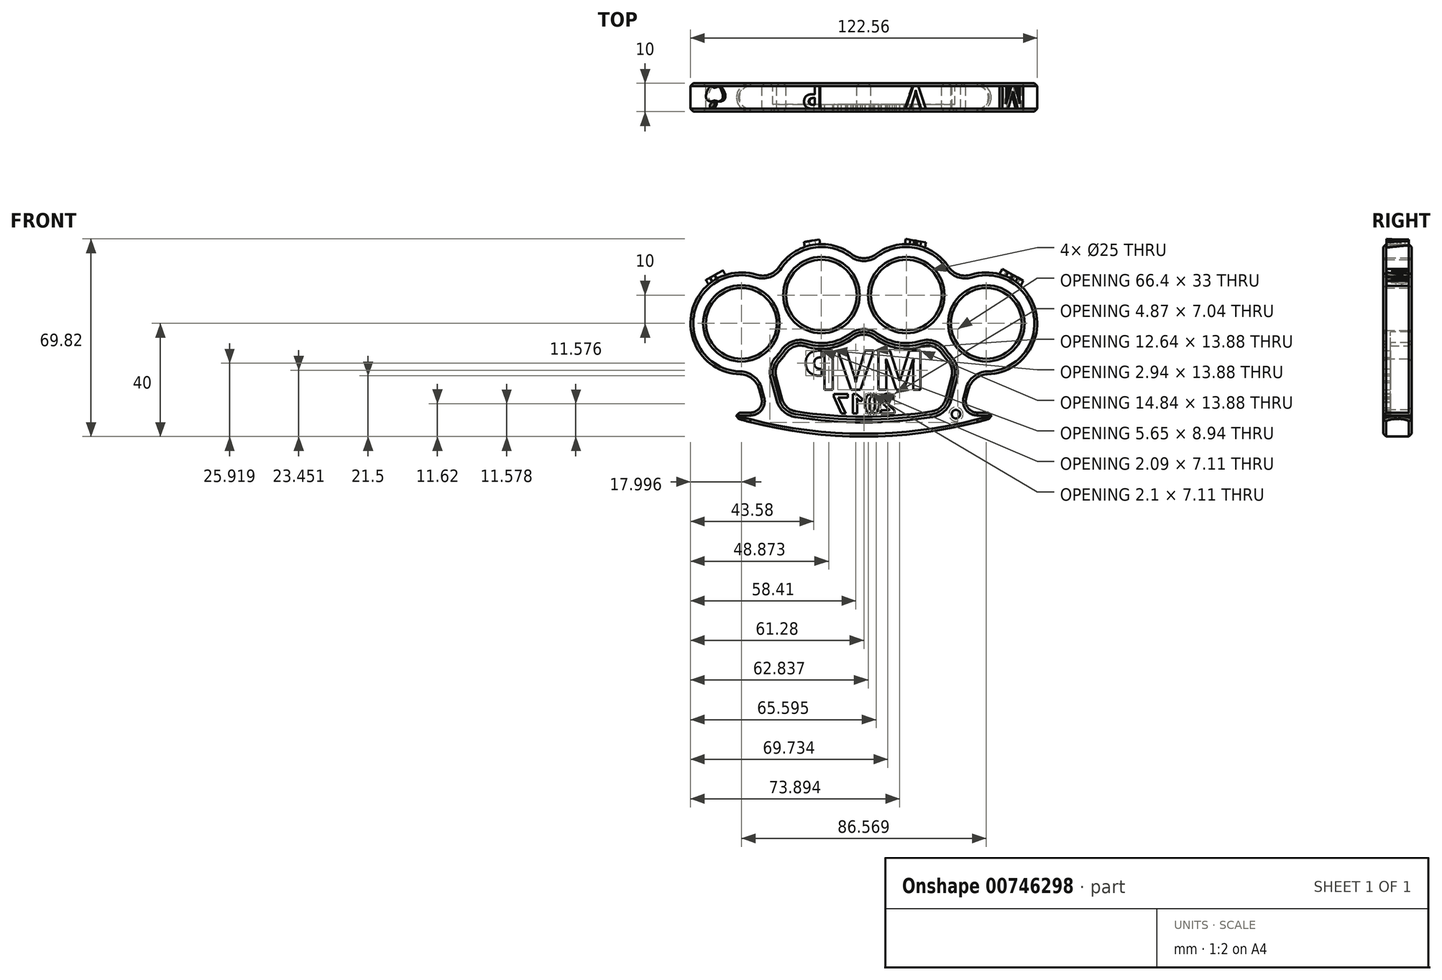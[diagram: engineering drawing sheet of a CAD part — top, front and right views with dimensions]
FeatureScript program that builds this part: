
annotation { "Feature Type Name" : "Feature", "Feature Type Description" : "" }
export const myFeature = defineFeature(function(context is Context, id is Id, definition is map)
    precondition{}
    {
        {
            var Q0;
            Q0=qCreatedBy(makeId("Front.planeOp"),FACE);
            var sketch = newSketch(context, id + "F0", { "sketchPlane" : qUnion([Q0])});
            skCircle(sketch, "E0", {"center": v(-43.28, 0) * mm, "radius": 12.5 * mm});
            skCircle(sketch, "E1", {"center": v(-15, 10) * mm, "radius": 12.5 * mm});
            skCircle(sketch, "E2", {"center": v(15, 10) * mm, "radius": 12.5 * mm});
            skCircle(sketch, "E3", {"center": v(43.28, 0) * mm, "radius": 12.5 * mm});
            skLineSegment(sketch, "E4", {"start": v(0, 38.87) * mm, "end": v(0, -56.1) * mm, "construction": true});
            skArc(sketch, "E5", {"start": v(-32.46, 14.38) * mm, "mid": v(-60.95, 3.43) * mm, "end": v(-38.63, -17.39) * mm});
            skArc(sketch, "E6", {"start": v(25.83, -4.38) * mm, "mid": v(28.5, -10.27) * mm, "end": v(33.1, -14.84) * mm});
            skArc(sketch, "E7.trimOffspring", {"start": v(-25.83, -4.38) * mm, "mid": v(-11.96, -7.74) * mm, "end": v(0, 0.05) * mm});
            skArc(sketch, "E8.trimOffspring", {"start": v(32.46, 14.38) * mm, "mid": v(18.04, 27.74) * mm, "end": v(0, 19.95) * mm});
            skArc(sketch, "E9.trimOffspring", {"start": v(0, 19.95) * mm, "mid": v(-18.04, 27.74) * mm, "end": v(-32.46, 14.38) * mm});
            skArc(sketch, "E10.trimOffspring", {"start": v(0, 0.05) * mm, "mid": v(11.96, -7.74) * mm, "end": v(25.83, -4.38) * mm});
            skArc(sketch, "E11", {"start": v(-45, -33.54) * mm, "mid": v(0, -40) * mm, "end": v(45, -33.54) * mm});
            skLineSegment(sketch, "E12", {"start": v(-45, -33.54) * mm, "end": v(-45, -31.54) * mm});
            skLineSegment(sketch, "E13", {"start": v(-36.18, -26.5) * mm, "end": v(-38.63, -17.39) * mm});
            skLineSegment(sketch, "E14", {"start": v(-45, -31.54) * mm, "end": v(-40.05, -31.54) * mm});
            skLineSegment(sketch, "E15.MirrorCS", {"start": v(45, -33.54) * mm, "end": v(45, -31.54) * mm});
            skPoint(sketch, "E16.visualSharp", {"position": v(-34.83, -31.54) * mm});
            skArc(sketch, "E16.filletArc", {"start": v(-40.05, -31.54) * mm, "mid": v(-36.87, -29.98) * mm, "end": v(-36.18, -26.5) * mm});
            skLineSegment(sketch, "E17.MirrorCS", {"start": v(36.18, -26.5) * mm, "end": v(38.63, -17.39) * mm});
            skLineSegment(sketch, "E18.MirrorCS", {"start": v(45, -31.54) * mm, "end": v(40.05, -31.54) * mm});
            skArc(sketch, "E19.MirrorCS", {"start": v(40.05, -31.54) * mm, "mid": v(36.87, -29.98) * mm, "end": v(36.18, -26.5) * mm});
            skArc(sketch, "E20", {"start": v(-28.68, -31.3) * mm, "mid": v(0, -34) * mm, "end": v(28.68, -31.3) * mm});
            skLineSegment(sketch, "E21", {"start": v(-28.68, -31.3) * mm, "end": v(-33.1, -14.84) * mm});
            skLineSegment(sketch, "E22", {"start": v(28.68, -31.3) * mm, "end": v(33.1, -14.84) * mm});
            skArc(sketch, "E23.trimOffspring", {"start": v(-33.1, -14.84) * mm, "mid": v(-28.5, -10.27) * mm, "end": v(-25.83, -4.38) * mm});
            skArc(sketch, "E24.trimOffspring", {"start": v(38.63, -17.39) * mm, "mid": v(60.95, 3.43) * mm, "end": v(32.46, 14.38) * mm});
            skSolve(sketch);
        }
        {
            var Q0;
            Q0=makeQuery(id+"F0.imprint","IMPRINT",FACE,{"disambiguationData":[TD([[makeQuery(id+"F0.imprint","IMPRINT",EDGE,{"derivedFrom":sQuery(id+"F0.wireOp",EDGE,"E0")}),-1.0]])]});
            extrude(context, id + "F1", {"entities" : qUnion([Q0]), "depth" : 10 * mm, "offsetDistance" : 25 * mm});
        }
        {
            var Q0;
            Q0=makeQuery(id+"F1.opExtrude","CAP_EDGE",EDGE,{"disambiguationData":[OSD([sQuery(id+"F0.wireOp",EDGE,"E12")])],"isStart":false});
            var Q1;
            Q1=makeQuery(id+"F1.opExtrude","CAP_EDGE",EDGE,{"disambiguationData":[OSD([sQuery(id+"F0.wireOp",EDGE,"E12")])],"isStart":true});
            var Q2;
            Q2=makeQuery(id+"F1.opExtrude","CAP_EDGE",EDGE,{"disambiguationData":[OSD([sQuery(id+"F0.wireOp",EDGE,"E15.MirrorCS")])],"isStart":false});
            var Q3;
            Q3=makeQuery(id+"F1.opExtrude","CAP_EDGE",EDGE,{"disambiguationData":[OSD([sQuery(id+"F0.wireOp",EDGE,"E15.MirrorCS")])],"isStart":true});
            fillet(context, id + "F2", {"entities" : qUnion([Q0, Q1, Q2, Q3]), "radius" : 5 * mm, "tangentPropagation" : true, "allowEdgeOverflow" : false});
        }
        {
            var Q0;
            Q0=makeQuery(id+"F1.opExtrude","SWEPT_EDGE",EDGE,{"disambiguationData":[OSD([sQuery(id+"F0.wireOp",EDGE,"E7.trimOffspring"),sQuery(id+"F0.wireOp",EDGE,"E23.trimOffspring")])]});
            var Q1;
            Q1=makeQuery(id+"F1.opExtrude","SWEPT_EDGE",EDGE,{"disambiguationData":[OSD([sQuery(id+"F0.wireOp",EDGE,"E7.trimOffspring"),sQuery(id+"F0.wireOp",EDGE,"E10.trimOffspring")])]});
            var Q2;
            Q2=makeQuery(id+"F1.opExtrude","SWEPT_EDGE",EDGE,{"disambiguationData":[OSD([sQuery(id+"F0.wireOp",EDGE,"E6"),sQuery(id+"F0.wireOp",EDGE,"E10.trimOffspring")])]});
            var Q3;
            Q3=makeQuery(id+"F1.opExtrude","SWEPT_EDGE",EDGE,{"disambiguationData":[OSD([sQuery(id+"F0.wireOp",EDGE,"E6"),sQuery(id+"F0.wireOp",EDGE,"E22")])]});
            var Q4;
            Q4=makeQuery(id+"F1.opExtrude","SWEPT_EDGE",EDGE,{"disambiguationData":[OSD([sQuery(id+"F0.wireOp",EDGE,"E21"),sQuery(id+"F0.wireOp",EDGE,"E23.trimOffspring")])]});
            var Q5;
            Q5=makeQuery(id+"F1.opExtrude","SWEPT_EDGE",EDGE,{"disambiguationData":[OSD([sQuery(id+"F0.wireOp",EDGE,"E8.trimOffspring"),sQuery(id+"F0.wireOp",EDGE,"E24.trimOffspring")])]});
            var Q6;
            Q6=makeQuery(id+"F1.opExtrude","SWEPT_EDGE",EDGE,{"disambiguationData":[OSD([sQuery(id+"F0.wireOp",EDGE,"E8.trimOffspring"),sQuery(id+"F0.wireOp",EDGE,"E9.trimOffspring")])]});
            var Q7;
            Q7=makeQuery(id+"F1.opExtrude","SWEPT_EDGE",EDGE,{"disambiguationData":[OSD([sQuery(id+"F0.wireOp",EDGE,"E5"),sQuery(id+"F0.wireOp",EDGE,"E9.trimOffspring")])]});
            var Q8;
            Q8=makeQuery(id+"F1.opExtrude","SWEPT_EDGE",EDGE,{"disambiguationData":[OSD([sQuery(id+"F0.wireOp",EDGE,"E20"),sQuery(id+"F0.wireOp",EDGE,"E21")])]});
            var Q9;
            Q9=makeQuery(id+"F1.opExtrude","SWEPT_EDGE",EDGE,{"disambiguationData":[OSD([sQuery(id+"F0.wireOp",EDGE,"E20"),sQuery(id+"F0.wireOp",EDGE,"E22")])]});
            var Q10;
            Q10=makeQuery(id+"F1.opExtrude","SWEPT_EDGE",EDGE,{"disambiguationData":[OSD([sQuery(id+"F0.wireOp",EDGE,"E5"),sQuery(id+"F0.wireOp",EDGE,"E13")])]});
            var Q11;
            Q11=makeQuery(id+"F1.opExtrude","SWEPT_EDGE",EDGE,{"disambiguationData":[OSD([sQuery(id+"F0.wireOp",EDGE,"E17.MirrorCS"),sQuery(id+"F0.wireOp",EDGE,"E24.trimOffspring")])]});
            fillet(context, id + "F3", {"entities" : qUnion([Q0, Q1, Q2, Q3, Q4, Q5, Q6, Q7, Q8, Q9, Q10, Q11]), "radius" : 7 * mm, "tangentPropagation" : true, "allowEdgeOverflow" : false});
        }
        {
            var Q0;
            Q0=qCreatedBy(makeId("Front.planeOp"),FACE);
            cPlane(context, id + "F4", {"entities" : qUnion([Q0]), "cplaneType" : CPlaneType.OFFSET, "offset" : 5 * mm, "width" : 150 * mm, "height" : 150 * mm});
        }
        {
            var Q0;
            Q0=makeQuery(id+"F1.opExtrude","CAP_FACE",FACE,{"disambiguationData":[OSD([sQuery(id+"F0.wireOp",EDGE,"E0"),sQuery(id+"F0.wireOp",EDGE,"E1"),sQuery(id+"F0.wireOp",EDGE,"E2"),sQuery(id+"F0.wireOp",EDGE,"E3"),sQuery(id+"F0.wireOp",EDGE,"E5"),sQuery(id+"F0.wireOp",EDGE,"E6"),sQuery(id+"F0.wireOp",EDGE,"E7.trimOffspring"),sQuery(id+"F0.wireOp",EDGE,"E8.trimOffspring"),sQuery(id+"F0.wireOp",EDGE,"E9.trimOffspring"),sQuery(id+"F0.wireOp",EDGE,"E10.trimOffspring"),sQuery(id+"F0.wireOp",EDGE,"E11"),sQuery(id+"F0.wireOp",EDGE,"E12"),sQuery(id+"F0.wireOp",EDGE,"E13"),sQuery(id+"F0.wireOp",EDGE,"E14"),sQuery(id+"F0.wireOp",EDGE,"E15.MirrorCS"),sQuery(id+"F0.wireOp",EDGE,"E16.filletArc"),sQuery(id+"F0.wireOp",EDGE,"E17.MirrorCS"),sQuery(id+"F0.wireOp",EDGE,"E18.MirrorCS"),sQuery(id+"F0.wireOp",EDGE,"E19.MirrorCS"),sQuery(id+"F0.wireOp",EDGE,"E20"),sQuery(id+"F0.wireOp",EDGE,"E21"),sQuery(id+"F0.wireOp",EDGE,"E22"),sQuery(id+"F0.wireOp",EDGE,"E23.trimOffspring"),sQuery(id+"F0.wireOp",EDGE,"E24.trimOffspring")])],"isStart":false});
            var sketch = newSketch(context, id + "F5", { "sketchPlane" : qUnion([Q0])});
            skLineSegment(sketch, "E25.0", {"start": v(-29.84, -26.99) * mm, "end": v(-31.96, -19.07) * mm});
            skArc(sketch, "E25.1", {"start": v(-24.18, -32.1) * mm, "mid": v(-27.76, -30.38) * mm, "end": v(-29.84, -26.99) * mm});
            skArc(sketch, "E25.2", {"start": v(-24.18, -32.1) * mm, "mid": v(0, -34) * mm, "end": v(24.18, -32.1) * mm});
            skArc(sketch, "E25.3", {"start": v(29.84, -26.99) * mm, "mid": v(27.76, -30.38) * mm, "end": v(24.18, -32.1) * mm});
            skLineSegment(sketch, "E25.4", {"start": v(29.84, -26.99) * mm, "end": v(31.96, -19.07) * mm});
            skArc(sketch, "E25.5", {"start": v(30.26, -12.43) * mm, "mid": v(31.98, -15.53) * mm, "end": v(31.96, -19.07) * mm});
            skArc(sketch, "E25.6", {"start": v(20.38, -7.18) * mm, "mid": v(24.8, -7.26) * mm, "end": v(28.3, -9.98) * mm});
            skArc(sketch, "E25.7", {"start": v(4.2, -4.4) * mm, "mid": v(11.96, -7.74) * mm, "end": v(20.38, -7.18) * mm});
            skArc(sketch, "E25.8", {"start": v(-4.2, -4.4) * mm, "mid": v(0, -3) * mm, "end": v(4.2, -4.4) * mm});
            skArc(sketch, "E25.9", {"start": v(-20.38, -7.18) * mm, "mid": v(-11.96, -7.74) * mm, "end": v(-4.2, -4.4) * mm});
            skArc(sketch, "E25.10", {"start": v(-28.3, -9.98) * mm, "mid": v(-24.8, -7.26) * mm, "end": v(-20.38, -7.18) * mm});
            skArc(sketch, "E25.11", {"start": v(-31.96, -19.07) * mm, "mid": v(-31.98, -15.53) * mm, "end": v(-30.26, -12.43) * mm});
            skArc(sketch, "E25.12", {"start": v(-30.26, -12.43) * mm, "mid": v(-29.23, -11.25) * mm, "end": v(-28.3, -9.98) * mm});
            skArc(sketch, "E25.13", {"start": v(28.3, -9.98) * mm, "mid": v(29.23, -11.25) * mm, "end": v(30.26, -12.43) * mm});
            skSolve(sketch);
        }
        {
            var Q0;
            Q0=qSketchRegion(id+"F5",true);
            extrude(context, id + "F6", {"entities" : qUnion([Q0]), "operationType" : NewBodyOperationType.ADD, "oppositeDirection" : true, "depth" : 2.5 * mm, "offsetDistance" : 25 * mm});
        }
        {
            var Q0;
            Q0=makeQuery(id+"F6.opExtrude","CAP_FACE",FACE,{"disambiguationData":[OSD([sQuery(id+"F5.wireOp",EDGE,"E25.0"),sQuery(id+"F5.wireOp",EDGE,"E25.1"),sQuery(id+"F5.wireOp",EDGE,"E25.2"),sQuery(id+"F5.wireOp",EDGE,"E25.3"),sQuery(id+"F5.wireOp",EDGE,"E25.4"),sQuery(id+"F5.wireOp",EDGE,"E25.5"),sQuery(id+"F5.wireOp",EDGE,"E25.6"),sQuery(id+"F5.wireOp",EDGE,"E25.7"),sQuery(id+"F5.wireOp",EDGE,"E25.8"),sQuery(id+"F5.wireOp",EDGE,"E25.9"),sQuery(id+"F5.wireOp",EDGE,"E25.10"),sQuery(id+"F5.wireOp",EDGE,"E25.11"),sQuery(id+"F5.wireOp",EDGE,"E25.12"),sQuery(id+"F5.wireOp",EDGE,"E25.13")])],"isStart":false});
            var sketch = newSketch(context, id + "F7", { "sketchPlane" : qUnion([Q0])});
            skText(sketch, "E26", { "text": "MVP", "fontName": "OpenSans-Bold.ttf"});
            skText(sketch, "E27", { "text": "2017", "fontName": "OpenSans-Bold.ttf"});
            const initialGuessF7  = {"E26": [-0.02178, -0.02349, 1, 0, 0.014], "E27": [-0.01126, -0.0319, 1, 0, 0.007]};
            skSetInitialGuess(sketch, initialGuessF7);
            skSolve(sketch);
        }
        {
            var Q0;
            Q0=qSketchRegion(id+"F7",true);
            extrude(context, id + "F8", {"entities" : qUnion([Q0]), "operationType" : NewBodyOperationType.REMOVE, "oppositeDirection" : true, "depth" : 25 * mm, "offsetDistance" : 25 * mm});
        }
        {
            var Q0;
            Q0=makeQuery(id+"F1.opExtrude","CAP_EDGE",EDGE,{"disambiguationData":[OSD([sQuery(id+"F0.wireOp",EDGE,"E5")])],"isStart":false});
            var Q1;
            Q1=makeQuery(id+"F1.opExtrude","CAP_EDGE",EDGE,{"disambiguationData":[OSD([sQuery(id+"F0.wireOp",EDGE,"E11")])],"isStart":false});
            var Q2;
            Q2=makeQuery(id+"F1.opExtrude","CAP_EDGE",EDGE,{"disambiguationData":[OSD([sQuery(id+"F0.wireOp",EDGE,"E21")])],"isStart":false});
            var Q3;
            Q3=makeQuery(id+"F1.opExtrude","CAP_EDGE",EDGE,{"disambiguationData":[OSD([sQuery(id+"F0.wireOp",EDGE,"E0")])],"isStart":false});
            var Q4;
            Q4=makeQuery(id+"F1.opExtrude","CAP_EDGE",EDGE,{"disambiguationData":[OSD([sQuery(id+"F0.wireOp",EDGE,"E1")])],"isStart":false});
            var Q5;
            Q5=makeQuery(id+"F1.opExtrude","CAP_EDGE",EDGE,{"disambiguationData":[OSD([sQuery(id+"F0.wireOp",EDGE,"E2")])],"isStart":false});
            var Q6;
            Q6=makeQuery(id+"F1.opExtrude","CAP_EDGE",EDGE,{"disambiguationData":[OSD([sQuery(id+"F0.wireOp",EDGE,"E3")])],"isStart":false});
            var Q7;
            Q7=makeQuery(id+"F1.opExtrude","CAP_EDGE",EDGE,{"disambiguationData":[OSD([sQuery(id+"F0.wireOp",EDGE,"E3")])],"isStart":true});
            var Q8;
            Q8=makeQuery(id+"F1.opExtrude","CAP_EDGE",EDGE,{"disambiguationData":[OSD([sQuery(id+"F0.wireOp",EDGE,"E2")])],"isStart":true});
            var Q9;
            Q9=makeQuery(id+"F1.opExtrude","CAP_EDGE",EDGE,{"disambiguationData":[OSD([sQuery(id+"F0.wireOp",EDGE,"E1")])],"isStart":true});
            var Q10;
            Q10=makeQuery(id+"F1.opExtrude","CAP_EDGE",EDGE,{"disambiguationData":[OSD([sQuery(id+"F0.wireOp",EDGE,"E0")])],"isStart":true});
            var Q11;
            Q11=makeQuery(id+"F1.opExtrude","CAP_EDGE",EDGE,{"disambiguationData":[OSD([sQuery(id+"F0.wireOp",EDGE,"E22")])],"isStart":true});
            var Q12;
            Q12=makeQuery(id+"F6.opExtrude","CAP_EDGE",EDGE,{"disambiguationData":[OSD([sQuery(id+"F5.wireOp",EDGE,"E25.4")])],"isStart":true});
            var Q13;
            Q13=makeQuery(id+"F6.opExtrude","CAP_EDGE",EDGE,{"disambiguationData":[OSD([sQuery(id+"F5.wireOp",EDGE,"E25.5")])],"isStart":false});
            chamfer(context, id + "F9", {"entities" : qUnion([Q0, Q1, Q2, Q3, Q4, Q5, Q6, Q7, Q8, Q9, Q10, Q11, Q12, Q13]), "width" : 1 * mm, "tangentPropagation" : true});
        }
        {
            var Q0;
            Q0=qCreatedBy(id+"F4.planeOp",FACE);
            var sketch = newSketch(context, id + "F10", { "sketchPlane" : qUnion([Q0])});
            skLineSegment(sketch, "E28", {"start": v(0, -77.43) * mm, "end": v(19.89, 38.49) * mm, "construction": true});
            skLineSegment(sketch, "E29", {"start": v(0, 38.45) * mm, "end": v(0, -77.43) * mm, "construction": true});
            skLineSegment(sketch, "E30", {"start": v(0, -77.43) * mm, "end": v(-64.72, 38.35) * mm, "construction": true});
            skLineSegment(sketch, "E31", {"start": v(0, -77.43) * mm, "end": v(63.92, 36.9) * mm, "construction": true});
            skCircle(sketch, "E32.0", {"center": v(-43.28, 0) * mm, "radius": 12.5 * mm});
            skCircle(sketch, "E33.0", {"center": v(43.28, 0) * mm, "radius": 12.5 * mm});
            skPoint(sketch, "E34", {"position": v(-52.07, 15.71) * mm});
            skPoint(sketch, "E35", {"position": v(-18.04, 27.74) * mm});
            skPoint(sketch, "E36", {"position": v(18.04, 27.74) * mm});
            skPoint(sketch, "E37", {"position": v(52.07, 15.71) * mm});
            skLineSegment(sketch, "E38", {"start": v(0, -77.43) * mm, "end": v(-21.26, 46.47) * mm, "construction": true});
            skCircle(sketch, "E39.0", {"center": v(-15, 10) * mm, "radius": 12.5 * mm});
            skSolve(sketch);
        }
        {
            var Q0;
            Q0=sQuery(id+"F10.wireOp",VERTEX,"E34");
            var Q1;
            Q1=sQuery(id+"F10.wireOp",EDGE,"E30");
            cPlane(context, id + "F11", {"entities" : qUnion([Q0, Q1]), "cplaneType" : CPlaneType.LINE_POINT, "offset" : 25 * mm, "width" : 150 * mm, "height" : 150 * mm});
        }
        {
            var Q0;
            Q0=sQuery(id+"F10.wireOp",EDGE,"E38");
            var Q1;
            Q1=sQuery(id+"F10.wireOp",VERTEX,"E35");
            cPlane(context, id + "F12", {"entities" : qUnion([Q0, Q1]), "cplaneType" : CPlaneType.LINE_POINT, "offset" : 25 * mm, "width" : 150 * mm, "height" : 150 * mm});
        }
        {
            var Q0;
            Q0=sQuery(id+"F10.wireOp",VERTEX,"E36");
            var Q1;
            Q1=sQuery(id+"F10.wireOp",EDGE,"E28");
            cPlane(context, id + "F13", {"entities" : qUnion([Q0, Q1]), "cplaneType" : CPlaneType.LINE_POINT, "offset" : 25 * mm, "width" : 150 * mm, "height" : 150 * mm});
        }
        {
            var Q0;
            Q0=sQuery(id+"F10.wireOp",VERTEX,"E37");
            var Q1;
            Q1=sQuery(id+"F10.wireOp",EDGE,"E31");
            cPlane(context, id + "F14", {"entities" : qUnion([Q0, Q1]), "cplaneType" : CPlaneType.LINE_POINT, "offset" : 25 * mm, "width" : 150 * mm, "height" : 150 * mm});
        }
        {
            var Q0;
            Q0=qCreatedBy(id+"F14.planeOp",FACE);
            var sketch = newSketch(context, id + "F15", { "sketchPlane" : qUnion([Q0])});
            skText(sketch, "E40", { "text": "M", "fontName": "OpenSans-Bold.ttf"});
            skLineSegment(sketch, "E41", {"start": v(42.88, -1) * mm, "end": v(73.13, -1) * mm});
            const initialGuessF15  = {"E40": [0.04288, -0.001, -1, 0, 0.008]};
            skSetInitialGuess(sketch, initialGuessF15);
            skSolve(sketch);
        }
        {
            var Q0;
            Q0=qCreatedBy(id+"F13.planeOp",FACE);
            var sketch = newSketch(context, id + "F16", { "sketchPlane" : qUnion([Q0])});
            skText(sketch, "E42", { "text": "V", "fontName": "OpenSans-Bold.ttf"});
            skLineSegment(sketch, "E43", {"start": v(13.53, -1) * mm, "end": v(16.76, -1) * mm});
            const initialGuessF16  = {"E42": [0.01676, -0.001, -1, 0, 0.008]};
            skSetInitialGuess(sketch, initialGuessF16);
            skSolve(sketch);
        }
        {
            var Q0;
            Q0=qCreatedBy(id+"F12.planeOp",FACE);
            var sketch = newSketch(context, id + "F17", { "sketchPlane" : qUnion([Q0])});
            skText(sketch, "E44", { "text": "P", "fontName": "OpenSans-Bold.ttf"});
            skLineSegment(sketch, "E45", {"start": v(-9.5, -1) * mm, "end": v(27.08, -1) * mm});
            const initialGuessF17  = {"E44": [-0.0095, -0.001, -1, 0, 0.008]};
            skSetInitialGuess(sketch, initialGuessF17);
            skSolve(sketch);
        }
        {
            var Q0;
            Q0=qCreatedBy(id+"F11.planeOp",FACE);
            var sketch = newSketch(context, id + "F18", { "sketchPlane" : qUnion([Q0])});
            skLineSegment(sketch, "E46", {"start": v(-37.78, 4.33) * mm, "end": v(-37.78, -21.33) * mm, "construction": true});
            skFitSpline(sketch, "E47", {"points": [v(-37.78, -1.74) * mm, v(-39.38, -1.13) * mm, v(-40.33, -2.03) * mm, v(-41.18, -4.15) * mm, v(-40.94, -5.57) * mm, v(-39.59, -6.37) * mm, v(-37.78, -6) * mm], "startDerivative": vector(-11.84, 8.82) * mm, "endDerivative": vector(10.4, 4.73) * mm});
            skPoint(sketch, "E48", {"position": v(-37.78, -8.5) * mm});
            skFitSpline(sketch, "E49.MirrorCS", {"points": [v(-37.78, -1.74) * mm, v(-36.18, -1.13) * mm, v(-35.23, -2.03) * mm, v(-34.38, -4.15) * mm, v(-34.63, -5.57) * mm, v(-35.97, -6.37) * mm, v(-37.78, -6) * mm], "startDerivative": vector(11.84, 8.82) * mm, "endDerivative": vector(-10.4, 4.73) * mm});
            skArc(sketch, "E50.filletArc", {"start": v(-38.29, -1.4) * mm, "mid": v(-37.78, -1.54) * mm, "end": v(-37.27, -1.4) * mm});
            skArc(sketch, "E51.filletArc", {"start": v(-37.43, -6.16) * mm, "mid": v(-37.78, -6.1) * mm, "end": v(-38.13, -6.16) * mm});
            skArc(sketch, "E52", {"start": v(-37.78, -6.5) * mm, "mid": v(-39.26, -7.12) * mm, "end": v(-39.57, -8.7) * mm});
            skArc(sketch, "E53", {"start": v(-39.57, -8.7) * mm, "mid": v(-38.07, -8.1) * mm, "end": v(-37.78, -6.5) * mm});
            skSolve(sketch);
        }
        {
            var Q0;
            Q0=qSketchRegion(id+"F18",true);
            extrude(context, id + "F19", {"entities" : qUnion([Q0]), "operationType" : NewBodyOperationType.ADD, "depth" : 1.5 * mm, "offsetDistance" : 25 * mm, "hasSecondDirection" : true, "secondDirectionBound" : SecondDirectionBoundingType.UP_TO_NEXT, "secondDirectionOppositeDirection" : true, "secondDirectionDepth" : 25 * mm});
        }
        {
            var Q0;
            Q0=qSketchRegion(id+"F17",true);
            extrude(context, id + "F20", {"entities" : qUnion([Q0]), "operationType" : NewBodyOperationType.ADD, "depth" : 1.5 * mm, "offsetDistance" : 25 * mm, "hasSecondDirection" : true, "secondDirectionBound" : SecondDirectionBoundingType.UP_TO_NEXT, "secondDirectionOppositeDirection" : true, "secondDirectionDepth" : 25 * mm});
        }
        {
            var Q0;
            Q0=qSketchRegion(id+"F16",true);
            extrude(context, id + "F21", {"entities" : qUnion([Q0]), "operationType" : NewBodyOperationType.ADD, "depth" : 1.5 * mm, "offsetDistance" : 25 * mm, "hasSecondDirection" : true, "secondDirectionBound" : SecondDirectionBoundingType.UP_TO_NEXT, "secondDirectionOppositeDirection" : true, "secondDirectionDepth" : 25 * mm});
        }
        {
            var Q0;
            Q0=qSketchRegion(id+"F15",true);
            extrude(context, id + "F22", {"entities" : qUnion([Q0]), "operationType" : NewBodyOperationType.ADD, "depth" : 1.5 * mm, "offsetDistance" : 25 * mm, "hasSecondDirection" : true, "secondDirectionBound" : SecondDirectionBoundingType.UP_TO_NEXT, "secondDirectionOppositeDirection" : true, "secondDirectionDepth" : 25 * mm});
        }
        {
            var Q0;
            Q0=makeQuery(id+"F1.opExtrude","CAP_FACE",FACE,{"disambiguationData":[OSD([sQuery(id+"F0.wireOp",EDGE,"E0"),sQuery(id+"F0.wireOp",EDGE,"E1"),sQuery(id+"F0.wireOp",EDGE,"E2"),sQuery(id+"F0.wireOp",EDGE,"E3"),sQuery(id+"F0.wireOp",EDGE,"E5"),sQuery(id+"F0.wireOp",EDGE,"E6"),sQuery(id+"F0.wireOp",EDGE,"E7.trimOffspring"),sQuery(id+"F0.wireOp",EDGE,"E8.trimOffspring"),sQuery(id+"F0.wireOp",EDGE,"E9.trimOffspring"),sQuery(id+"F0.wireOp",EDGE,"E10.trimOffspring"),sQuery(id+"F0.wireOp",EDGE,"E11"),sQuery(id+"F0.wireOp",EDGE,"E12"),sQuery(id+"F0.wireOp",EDGE,"E13"),sQuery(id+"F0.wireOp",EDGE,"E14"),sQuery(id+"F0.wireOp",EDGE,"E15.MirrorCS"),sQuery(id+"F0.wireOp",EDGE,"E16.filletArc"),sQuery(id+"F0.wireOp",EDGE,"E17.MirrorCS"),sQuery(id+"F0.wireOp",EDGE,"E18.MirrorCS"),sQuery(id+"F0.wireOp",EDGE,"E19.MirrorCS"),sQuery(id+"F0.wireOp",EDGE,"E20"),sQuery(id+"F0.wireOp",EDGE,"E21"),sQuery(id+"F0.wireOp",EDGE,"E22"),sQuery(id+"F0.wireOp",EDGE,"E23.trimOffspring"),sQuery(id+"F0.wireOp",EDGE,"E24.trimOffspring")])],"isStart":false});
            var sketch = newSketch(context, id + "F23", { "sketchPlane" : qUnion([Q0])});
            skCircle(sketch, "E54", {"center": v(32.55, -32.09) * mm, "radius": 1.5 * mm});
            skSolve(sketch);
        }
        {
            var Q0;
            Q0=makeQuery(id+"F23.imprint","IMPRINT",FACE,{"disambiguationData":[TD([[makeQuery(id+"F23.imprint","IMPRINT",EDGE,{"derivedFrom":sQuery(id+"F23.wireOp",EDGE,"E54")}),1.0]])]});
            extrude(context, id + "F24", {"entities" : qUnion([Q0]), "operationType" : NewBodyOperationType.REMOVE, "oppositeDirection" : true, "depth" : 25 * mm, "offsetDistance" : 25 * mm});
        }
        {
            var Q0;
            Q0=makeQuery(id+"F24.boolean.opBoolean","COPY",EDGE,{"derivedFrom":makeQuery(id+"F24.opExtrude","CAP_EDGE",EDGE,{"disambiguationData":[OSD([sQuery(id+"F23.wireOp",EDGE,"E54")])],"isStart":true})});
            var Q1;
            Q1=makeQuery(id+"F24.boolean.opBoolean","INTERSECT",EDGE,{"derivedFrom":[makeQuery(id+"F1.opExtrude","CAP_FACE",FACE,{"disambiguationData":[OSD([sQuery(id+"F0.wireOp",EDGE,"E0"),sQuery(id+"F0.wireOp",EDGE,"E1"),sQuery(id+"F0.wireOp",EDGE,"E2"),sQuery(id+"F0.wireOp",EDGE,"E3"),sQuery(id+"F0.wireOp",EDGE,"E5"),sQuery(id+"F0.wireOp",EDGE,"E6"),sQuery(id+"F0.wireOp",EDGE,"E7.trimOffspring"),sQuery(id+"F0.wireOp",EDGE,"E8.trimOffspring"),sQuery(id+"F0.wireOp",EDGE,"E9.trimOffspring"),sQuery(id+"F0.wireOp",EDGE,"E10.trimOffspring"),sQuery(id+"F0.wireOp",EDGE,"E11"),sQuery(id+"F0.wireOp",EDGE,"E12"),sQuery(id+"F0.wireOp",EDGE,"E13"),sQuery(id+"F0.wireOp",EDGE,"E14"),sQuery(id+"F0.wireOp",EDGE,"E15.MirrorCS"),sQuery(id+"F0.wireOp",EDGE,"E16.filletArc"),sQuery(id+"F0.wireOp",EDGE,"E17.MirrorCS"),sQuery(id+"F0.wireOp",EDGE,"E18.MirrorCS"),sQuery(id+"F0.wireOp",EDGE,"E19.MirrorCS"),sQuery(id+"F0.wireOp",EDGE,"E20"),sQuery(id+"F0.wireOp",EDGE,"E21"),sQuery(id+"F0.wireOp",EDGE,"E22"),sQuery(id+"F0.wireOp",EDGE,"E23.trimOffspring"),sQuery(id+"F0.wireOp",EDGE,"E24.trimOffspring")])],"isStart":true}),makeQuery(id+"F24.opExtrude","SWEPT_FACE",FACE,{"disambiguationData":[OSD([sQuery(id+"F23.wireOp",EDGE,"E54")])]})]});
            chamfer(context, id + "F25", {"entities" : qUnion([Q0, Q1]), "width" : 1 * mm, "tangentPropagation" : true});
        }
        {
            var Q0;
            {var subQ6=sQuery(id+"F0.wireOp",EDGE,"E6");Q0=makeQuery(id+"F8.boolean.opBoolean","SPLIT",FACE,{"disambiguationData":[TD([makeQuery(id+"F1.opExtrude","SWEPT_FACE",FACE,{"disambiguationData":[OSD([subQ6])]})])],"derivedFrom":makeQuery(id+"F6.opExtrude","CAP_FACE",FACE,{"disambiguationData":[OSD([sQuery(id+"F5.wireOp",EDGE,"E25.0"),sQuery(id+"F5.wireOp",EDGE,"E25.1"),sQuery(id+"F5.wireOp",EDGE,"E25.2"),sQuery(id+"F5.wireOp",EDGE,"E25.3"),sQuery(id+"F5.wireOp",EDGE,"E25.4"),sQuery(id+"F5.wireOp",EDGE,"E25.5"),sQuery(id+"F5.wireOp",EDGE,"E25.6"),sQuery(id+"F5.wireOp",EDGE,"E25.7"),sQuery(id+"F5.wireOp",EDGE,"E25.8"),sQuery(id+"F5.wireOp",EDGE,"E25.9"),sQuery(id+"F5.wireOp",EDGE,"E25.10"),sQuery(id+"F5.wireOp",EDGE,"E25.11"),sQuery(id+"F5.wireOp",EDGE,"E25.12"),sQuery(id+"F5.wireOp",EDGE,"E25.13")])],"isStart":false})});}
            var sketch = newSketch(context, id + "F26", { "sketchPlane" : qUnion([Q0])});
            skLineSegment(sketch, "E55", {"start": v(13.88, -18.55) * mm, "end": v(13.88, -9.6) * mm});
            skLineSegment(sketch, "E56", {"start": v(13.88, -9.6) * mm, "end": v(14.88, -9.6) * mm});
            skLineSegment(sketch, "E57", {"start": v(14.88, -9.6) * mm, "end": v(14.88, -18.55) * mm});
            skLineSegment(sketch, "E58", {"start": v(15.14, -18.55) * mm, "end": v(13.88, -18.55) * mm});
            skLineSegment(sketch, "E59.bottom", {"start": v(-3.27, -24.64) * mm, "end": v(-2.6, -24.64) * mm});
            skLineSegment(sketch, "E59.top", {"start": v(-3.27, -32.5) * mm, "end": v(-2.6, -32.5) * mm});
            skLineSegment(sketch, "E59.left", {"start": v(-3.27, -24.64) * mm, "end": v(-3.27, -32.5) * mm});
            skLineSegment(sketch, "E59.right", {"start": v(-2.6, -24.64) * mm, "end": v(-2.6, -32.5) * mm});
            skLineSegment(sketch, "E60", {"start": v(-2.94, -23.5) * mm, "end": v(-2.94, -36.08) * mm, "construction": true});
            skSolve(sketch);
        }
        {
            var Q0;
            Q0=qSketchRegion(id+"F26",true);
            var Q1;
            {var subQ0=sQuery(id+"F0.wireOp",EDGE,"E17.MirrorCS");var subQ1=sQuery(id+"F0.wireOp",EDGE,"E9.trimOffspring");var subQ2=sQuery(id+"F0.wireOp",EDGE,"E5");var subQ3=sQuery(id+"F0.wireOp",EDGE,"E24.trimOffspring");var subQ4=sQuery(id+"F0.wireOp",EDGE,"E8.trimOffspring");var subQ5=sQuery(id+"F0.wireOp",EDGE,"E12");var subQ6=sQuery(id+"F0.wireOp",EDGE,"E13");var subQ7=sQuery(id+"F0.wireOp",EDGE,"E2");var subQ8=sQuery(id+"F0.wireOp",EDGE,"E15.MirrorCS");var subQ9=sQuery(id+"F0.wireOp",EDGE,"E1");var subQ10=sQuery(id+"F0.wireOp",EDGE,"E19.MirrorCS");var subQ11=sQuery(id+"F0.wireOp",EDGE,"E3");var subQ12=sQuery(id+"F0.wireOp",EDGE,"E0");var subQ13=sQuery(id+"F0.wireOp",EDGE,"E16.filletArc");var subQ14=sQuery(id+"F0.wireOp",EDGE,"E11");Q1=makeQuery(id+"F8.boolean.opBoolean","SPLIT",FACE,{"disambiguationData":[TD([makeQuery(id+"F1.opExtrude","SWEPT_FACE",FACE,{"disambiguationData":[OSD([subQ12])]})])],"derivedFrom":makeQuery(id+"F6.boolean.opBoolean","MERGE",FACE,{"derivedFrom":[makeQuery(id+"F1.opExtrude","CAP_FACE",FACE,{"disambiguationData":[OSD([subQ12,subQ9,subQ7,subQ11,subQ2,sQuery(id+"F0.wireOp",EDGE,"E6"),sQuery(id+"F0.wireOp",EDGE,"E7.trimOffspring"),subQ4,subQ1,sQuery(id+"F0.wireOp",EDGE,"E10.trimOffspring"),subQ14,subQ5,subQ6,sQuery(id+"F0.wireOp",EDGE,"E14"),subQ8,subQ13,subQ0,sQuery(id+"F0.wireOp",EDGE,"E18.MirrorCS"),subQ10,sQuery(id+"F0.wireOp",EDGE,"E20"),sQuery(id+"F0.wireOp",EDGE,"E21"),sQuery(id+"F0.wireOp",EDGE,"E22"),sQuery(id+"F0.wireOp",EDGE,"E23.trimOffspring"),subQ3])],"isStart":true}),makeQuery(id+"F6.opExtrude","CAP_FACE",FACE,{"disambiguationData":[OSD([sQuery(id+"F5.wireOp",EDGE,"E25.0"),sQuery(id+"F5.wireOp",EDGE,"E25.1"),sQuery(id+"F5.wireOp",EDGE,"E25.2"),sQuery(id+"F5.wireOp",EDGE,"E25.3"),sQuery(id+"F5.wireOp",EDGE,"E25.4"),sQuery(id+"F5.wireOp",EDGE,"E25.5"),sQuery(id+"F5.wireOp",EDGE,"E25.6"),sQuery(id+"F5.wireOp",EDGE,"E25.7"),sQuery(id+"F5.wireOp",EDGE,"E25.8"),sQuery(id+"F5.wireOp",EDGE,"E25.9"),sQuery(id+"F5.wireOp",EDGE,"E25.10"),sQuery(id+"F5.wireOp",EDGE,"E25.11"),sQuery(id+"F5.wireOp",EDGE,"E25.12"),sQuery(id+"F5.wireOp",EDGE,"E25.13")])],"isStart":true})]})});}
            extrude(context, id + "F27", {"entities" : qUnion([Q0]), "operationType" : NewBodyOperationType.ADD, "endBound" : BoundingType.UP_TO_SURFACE, "oppositeDirection" : true, "depth" : 25 * mm, "endBoundEntityFace" : qUnion([Q1]), "offsetDistance" : 25 * mm});
        }
        {
            var Q0;
            {var subQ0=sQuery(id+"F5.wireOp",EDGE,"E25.13");var subQ1=sQuery(id+"F5.wireOp",EDGE,"E25.12");var subQ2=sQuery(id+"F5.wireOp",EDGE,"E25.11");var subQ3=sQuery(id+"F5.wireOp",EDGE,"E25.10");var subQ4=sQuery(id+"F5.wireOp",EDGE,"E25.9");var subQ5=sQuery(id+"F5.wireOp",EDGE,"E25.8");var subQ6=sQuery(id+"F5.wireOp",EDGE,"E25.7");var subQ7=sQuery(id+"F5.wireOp",EDGE,"E25.6");var subQ8=sQuery(id+"F5.wireOp",EDGE,"E25.5");var subQ9=sQuery(id+"F5.wireOp",EDGE,"E25.4");var subQ10=sQuery(id+"F5.wireOp",EDGE,"E25.3");var subQ11=sQuery(id+"F5.wireOp",EDGE,"E25.2");var subQ12=sQuery(id+"F5.wireOp",EDGE,"E25.1");var subQ13=sQuery(id+"F5.wireOp",EDGE,"E25.0");var subQ14=sQuery(id+"F0.wireOp",EDGE,"E24.trimOffspring");var subQ15=sQuery(id+"F0.wireOp",EDGE,"E23.trimOffspring");var subQ16=sQuery(id+"F0.wireOp",EDGE,"E22");var subQ17=sQuery(id+"F0.wireOp",EDGE,"E21");var subQ18=sQuery(id+"F0.wireOp",EDGE,"E20");var subQ19=sQuery(id+"F0.wireOp",EDGE,"E19.MirrorCS");var subQ20=sQuery(id+"F0.wireOp",EDGE,"E18.MirrorCS");var subQ21=sQuery(id+"F0.wireOp",EDGE,"E17.MirrorCS");var subQ22=sQuery(id+"F0.wireOp",EDGE,"E16.filletArc");var subQ23=sQuery(id+"F0.wireOp",EDGE,"E15.MirrorCS");var subQ24=sQuery(id+"F0.wireOp",EDGE,"E14");var subQ25=sQuery(id+"F0.wireOp",EDGE,"E13");var subQ26=sQuery(id+"F0.wireOp",EDGE,"E12");var subQ27=sQuery(id+"F0.wireOp",EDGE,"E11");var subQ28=sQuery(id+"F0.wireOp",EDGE,"E10.trimOffspring");var subQ29=sQuery(id+"F0.wireOp",EDGE,"E9.trimOffspring");var subQ30=sQuery(id+"F0.wireOp",EDGE,"E8.trimOffspring");var subQ31=sQuery(id+"F0.wireOp",EDGE,"E7.trimOffspring");var subQ32=sQuery(id+"F0.wireOp",EDGE,"E6");var subQ33=sQuery(id+"F0.wireOp",EDGE,"E5");var subQ34=sQuery(id+"F0.wireOp",EDGE,"E3");var subQ35=sQuery(id+"F0.wireOp",EDGE,"E2");var subQ36=sQuery(id+"F0.wireOp",EDGE,"E1");var subQ37=sQuery(id+"F0.wireOp",EDGE,"E0");var subQ38=makeQuery(id+"F6.boolean.opBoolean","MERGE",FACE,{"derivedFrom":[makeQuery(id+"F1.opExtrude","CAP_FACE",FACE,{"disambiguationData":[OSD([subQ37,subQ36,subQ35,subQ34,subQ33,subQ32,subQ31,subQ30,subQ29,subQ28,subQ27,subQ26,subQ25,subQ24,subQ23,subQ22,subQ21,subQ20,subQ19,subQ18,subQ17,subQ16,subQ15,subQ14])],"isStart":true}),makeQuery(id+"F6.opExtrude","CAP_FACE",FACE,{"disambiguationData":[OSD([subQ13,subQ12,subQ11,subQ10,subQ9,subQ8,subQ7,subQ6,subQ5,subQ4,subQ3,subQ2,subQ1,subQ0])],"isStart":true})]});Q0=makeQuery(id+"F27.boolean.opBoolean","MERGE",FACE,{"derivedFrom":[makeQuery(id+"F8.boolean.opBoolean","SPLIT",FACE,{"disambiguationData":[TD([makeQuery(id+"F8.opExtrude","SWEPT_FACE",FACE,{"disambiguationData":[OSD([sQuery(id+"F7.wireOp",EDGE,"E26.sketch_text.stroke-29")])]})])],"derivedFrom":subQ38}),makeQuery(id+"F8.boolean.opBoolean","SPLIT",FACE,{"disambiguationData":[TD([makeQuery(id+"F8.opExtrude","SWEPT_FACE",FACE,{"disambiguationData":[OSD([sQuery(id+"F7.wireOp",EDGE,"E27.sketch_text.stroke-32")])]})])],"derivedFrom":subQ38}),makeQuery(id+"F8.boolean.opBoolean","SPLIT",FACE,{"disambiguationData":[TD([makeQuery(id+"F1.opExtrude","SWEPT_FACE",FACE,{"disambiguationData":[OSD([subQ37])]})])],"derivedFrom":subQ38}),makeQuery(id+"F27.opExtrude","CAP_FACE",FACE,{"disambiguationData":[OSD([subQ37,subQ36,subQ35,subQ34,subQ33,subQ32,subQ31,subQ30,subQ29,subQ28,subQ27,subQ26,subQ25,subQ24,subQ23,subQ22,subQ21,subQ20,subQ19,subQ18,subQ17,subQ16,subQ15,subQ14,subQ13,subQ12,subQ11,subQ10,subQ9,subQ8,subQ7,subQ6,subQ5,subQ4,subQ3,subQ2,subQ1,subQ0]),OD(0.0)],"isStart":false}),makeQuery(id+"F27.opExtrude","CAP_FACE",FACE,{"disambiguationData":[OSD([subQ37,subQ36,subQ35,subQ34,subQ33,subQ32,subQ31,subQ30,subQ29,subQ28,subQ27,subQ26,subQ25,subQ24,subQ23,subQ22,subQ21,subQ20,subQ19,subQ18,subQ17,subQ16,subQ15,subQ14,subQ13,subQ12,subQ11,subQ10,subQ9,subQ8,subQ7,subQ6,subQ5,subQ4,subQ3,subQ2,subQ1,subQ0]),OD(1.0)],"isStart":false})]});}
            var sketch = newSketch(context, id + "F28", { "sketchPlane" : qUnion([Q0])});
            skLineSegment(sketch, "E61.0", {"start": v(-31.96, -19.07) * mm, "end": v(-29.84, -26.99) * mm});
            skArc(sketch, "E62.0", {"start": v(-30.26, -12.43) * mm, "mid": v(-31.98, -15.53) * mm, "end": v(-31.96, -19.07) * mm});
            skArc(sketch, "E63.0", {"start": v(-28.3, -9.98) * mm, "mid": v(-29.23, -11.25) * mm, "end": v(-30.26, -12.43) * mm});
            skArc(sketch, "E64.0", {"start": v(-20.38, -7.18) * mm, "mid": v(-24.8, -7.26) * mm, "end": v(-28.3, -9.98) * mm});
            skArc(sketch, "E65.0", {"start": v(-4.2, -4.4) * mm, "mid": v(-11.96, -7.74) * mm, "end": v(-20.38, -7.18) * mm});
            skArc(sketch, "E66.0", {"start": v(4.2, -4.4) * mm, "mid": v(0, -3) * mm, "end": v(-4.2, -4.4) * mm});
            skArc(sketch, "E67.0", {"start": v(20.38, -7.18) * mm, "mid": v(11.96, -7.74) * mm, "end": v(4.2, -4.4) * mm});
            skArc(sketch, "E68.0", {"start": v(28.3, -9.98) * mm, "mid": v(24.8, -7.26) * mm, "end": v(20.38, -7.18) * mm});
            skArc(sketch, "E69.0", {"start": v(30.26, -12.43) * mm, "mid": v(29.23, -11.25) * mm, "end": v(28.3, -9.98) * mm});
            skArc(sketch, "E70.0", {"start": v(31.96, -19.07) * mm, "mid": v(31.98, -15.53) * mm, "end": v(30.26, -12.43) * mm});
            skLineSegment(sketch, "E71.0", {"start": v(29.84, -26.99) * mm, "end": v(31.96, -19.07) * mm});
            skArc(sketch, "E72.0", {"start": v(24.18, -32.1) * mm, "mid": v(27.76, -30.38) * mm, "end": v(29.84, -26.99) * mm});
            skArc(sketch, "E73.0", {"start": v(-24.18, -32.1) * mm, "mid": v(0, -34) * mm, "end": v(24.18, -32.1) * mm});
            skArc(sketch, "E74.0", {"start": v(-29.84, -26.99) * mm, "mid": v(-27.76, -30.38) * mm, "end": v(-24.18, -32.1) * mm});
            skSolve(sketch);
        }
        {
            var Q0;
            Q0=qCreatedBy(makeId("Right.planeOp"),FACE);
            var sketch = newSketch(context, id + "F29", { "sketchPlane" : qUnion([Q0])});
            skPoint(sketch, "E75", {"position": v(-4.23, -3) * mm});
            skLineSegment(sketch, "E76", {"start": v(-3.24, -3) * mm, "end": v(-12, -3) * mm, "construction": true});
            skLineSegment(sketch, "E77", {"start": v(-9, -3) * mm, "end": v(-10, -2) * mm});
            skLineSegment(sketch, "E78", {"start": v(-10, -2) * mm, "end": v(-10, -4) * mm});
            skLineSegment(sketch, "E79", {"start": v(-10, -4) * mm, "end": v(-9, -3) * mm});
            skSolve(sketch);
        }
        {
            var Q0;
            Q0=qSketchRegion(id+"F29",true);
            var Q1;
            Q1=qConstructionFilter(qBodyType(qCreatedBy(id+"F28",EDGE),BodyType.WIRE),ConstructionObject.NO);
            sweep(context, id + "F30", {"operationType" : NewBodyOperationType.REMOVE, "profiles" : qUnion([Q0]), "path" : qUnion([Q1])});
        }
    });
